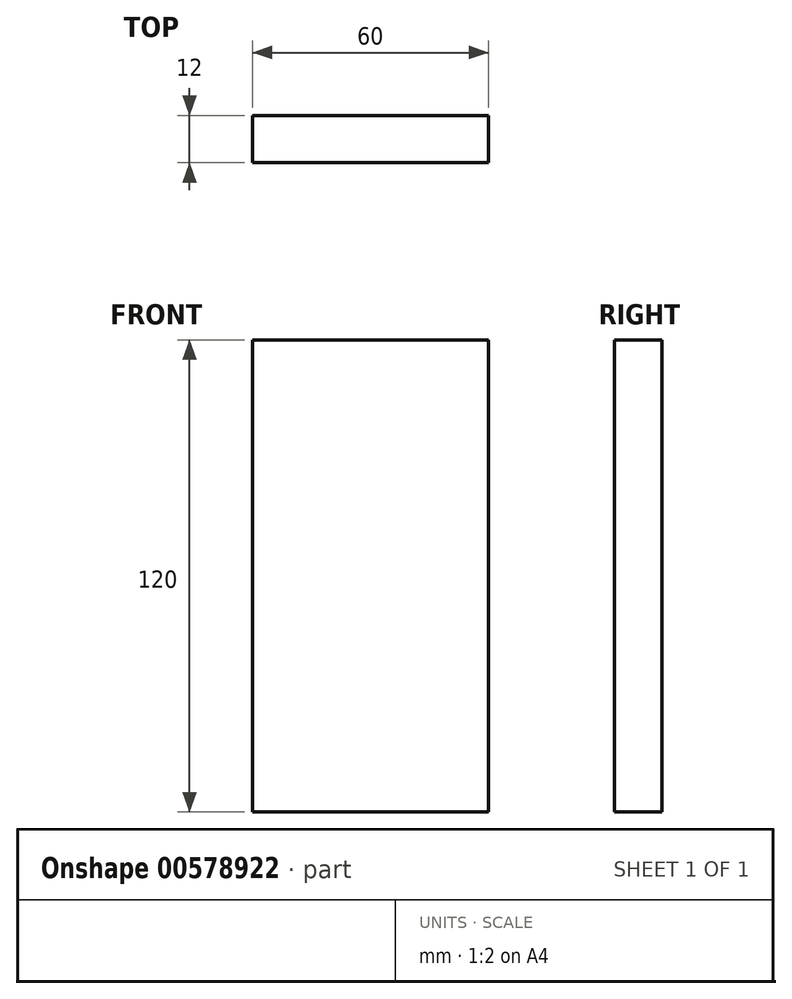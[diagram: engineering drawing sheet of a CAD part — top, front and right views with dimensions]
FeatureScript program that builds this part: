
annotation { "Feature Type Name" : "Feature", "Feature Type Description" : "" }
export const myFeature = defineFeature(function(context is Context, id is Id, definition is map)
    precondition{}
    {
        {
            var Q0;
            Q0=qCreatedBy(makeId("Front.planeOp"),FACE);
            var sketch = newSketch(context, id + "F0", { "sketchPlane" : qUnion([Q0])});
            skLineSegment(sketch, "E0.bottom", {"start": v(30, 60) * mm, "end": v(-30, 60) * mm});
            skLineSegment(sketch, "E0.top", {"start": v(30, -60) * mm, "end": v(-30, -60) * mm});
            skLineSegment(sketch, "E0.left", {"start": v(30, 60) * mm, "end": v(30, -60) * mm});
            skLineSegment(sketch, "E0.right", {"start": v(-30, 60) * mm, "end": v(-30, -60) * mm});
            skPoint(sketch, "E0.middle", {"position": v(0, 0) * mm});
            skSolve(sketch);
        }
        {
            var Q0;
            Q0 = qSketchRegion(id + "F0", true);
            extrude(context, id + "F1", {"entities" : qUnion([Q0]), "depth" : 12 * mm, "offsetDistance" : 25 * mm});
        }
    });
